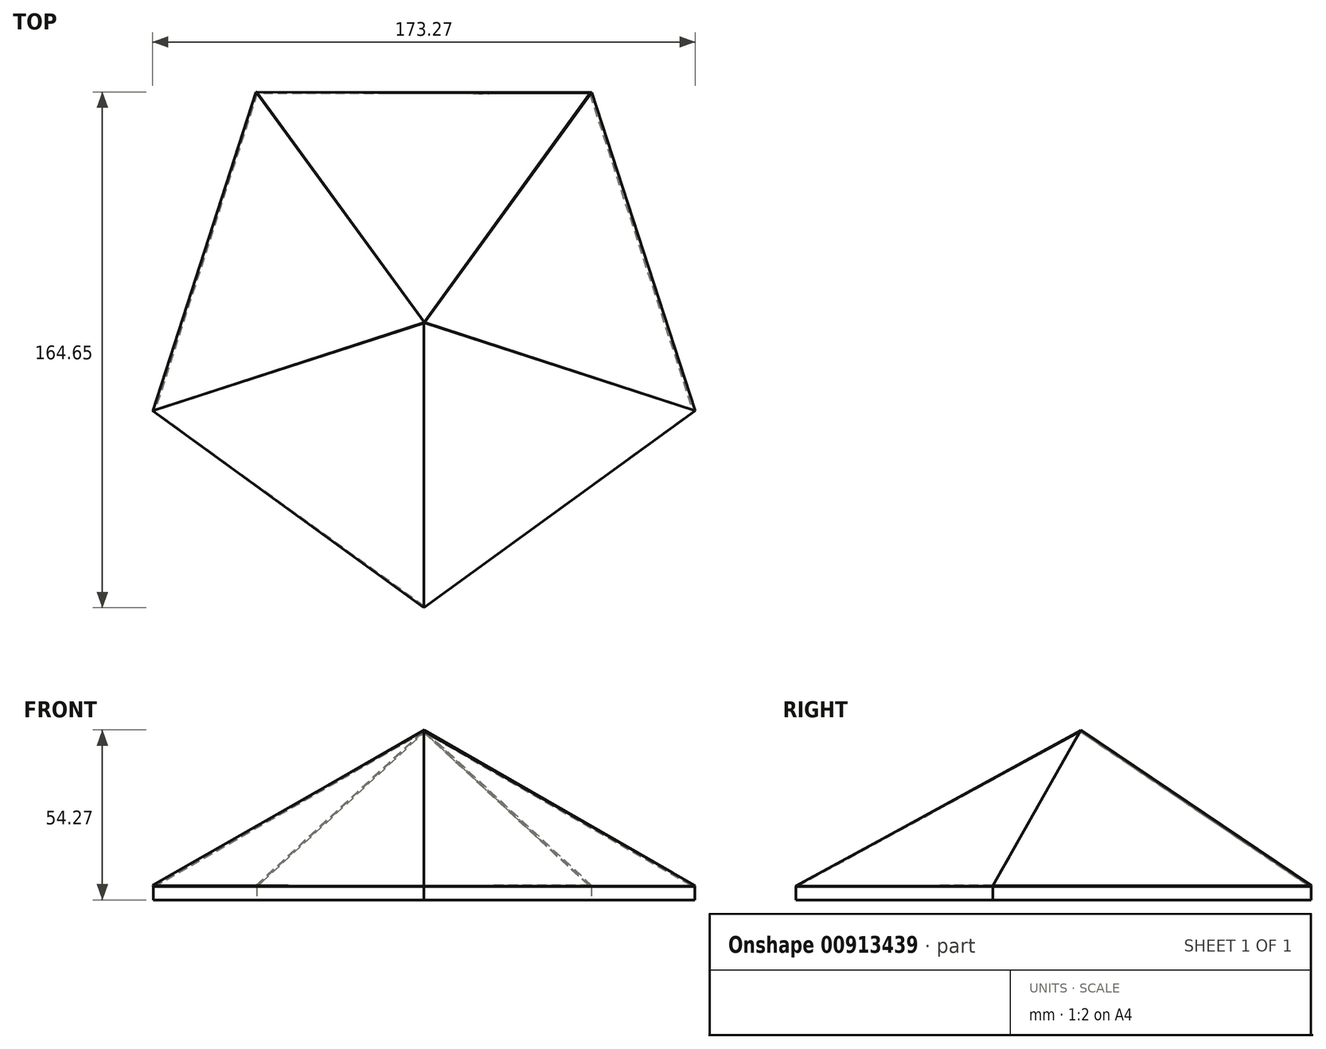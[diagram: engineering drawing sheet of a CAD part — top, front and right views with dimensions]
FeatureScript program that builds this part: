
annotation { "Feature Type Name" : "Feature", "Feature Type Description" : "" }
export const myFeature = defineFeature(function(context is Context, id is Id, definition is map)
    precondition{}
    {
        {
            var Q0;
            Q0=qCreatedBy(makeId("Top.planeOp"),FACE);
            var sketch = newSketch(context, id + "F0", { "sketchPlane" : qUnion([Q0])});
            skCircle(sketch, "E0.cCircle", {"center": v(0, 0) * mm, "radius": 73.52 * mm, "construction": true});
            skLineSegment(sketch, "E0.0", {"start": v(-53.41, 73.52) * mm, "end": v(53.41, 73.52) * mm});
            skLineSegment(sketch, "E0.1", {"start": v(53.41, 73.52) * mm, "end": v(86.43, -28.08) * mm});
            skLineSegment(sketch, "E0.2", {"start": v(86.43, -28.08) * mm, "end": v(0, -90.87) * mm});
            skLineSegment(sketch, "E0.3", {"start": v(0, -90.87) * mm, "end": v(-86.43, -28.08) * mm});
            skLineSegment(sketch, "E0.4", {"start": v(-86.43, -28.08) * mm, "end": v(-53.41, 73.52) * mm});
            skPoint(sketch, "E0.0.midPoint", {"position": v(0, 73.52) * mm});
            skSolve(sketch);
        }
        {
            var Q0;
            Q0=qCreatedBy(makeId("Front.planeOp"),FACE);
            var sketch = newSketch(context, id + "F1", { "sketchPlane" : qUnion([Q0])});
            skLineSegment(sketch, "E1", {"start": v(0, 0) * mm, "end": v(0, 53.85) * mm});
            skSolve(sketch);
        }
        {
            var Q0;
            Q0=makeQuery(id+"F0.imprint","IMPRINT",FACE,{"disambiguationData":[TD([[makeQuery(id+"F0.imprint","IMPRINT",EDGE,{"derivedFrom":sQuery(id+"F0.wireOp",EDGE,"E0.0")}),-1.0]])]});
            extrude(context, id + "F2", {"entities" : qUnion([Q0]), "depth" : 4.25 * mm, "offsetDistance" : 25.4 * mm});
        }
        {
            var Q0;
            Q0=makeQuery(id+"F2.opExtrude","CAP_VERTEX",VERTEX,{"disambiguationData":[OSD([sQuery(id+"F0.wireOp",EDGE,"E0.1"),sQuery(id+"F0.wireOp",EDGE,"E0.2")])],"isStart":false});
            var Q1;
            Q1=makeQuery(id+"F2.opExtrude","CAP_VERTEX",VERTEX,{"disambiguationData":[OSD([sQuery(id+"F0.wireOp",EDGE,"E0.0"),sQuery(id+"F0.wireOp",EDGE,"E0.1")])],"isStart":false});
            var Q2;
            Q2=sQuery(id+"F1.wireOp",VERTEX,"E1.end");
            cPlane(context, id + "F3", {"entities" : qUnion([Q0, Q1, Q2]), "cplaneType" : CPlaneType.THREE_POINT, "offset" : 25.4 * mm, "width" : 152.4 * mm, "height" : 152.4 * mm});
        }
        {
            var Q0;
            Q0=qCreatedBy(id+"F3.planeOp",FACE);
            var sketch = newSketch(context, id + "F4", { "sketchPlane" : qUnion([Q0])});
            skPoint(sketch, "E2.0", {"position": v(35.04, -71.1) * mm});
            skPoint(sketch, "E3.0", {"position": v(74.02, 28.36) * mm});
            skPoint(sketch, "E4.0", {"position": v(-28.04, 10.99) * mm});
            skLineSegment(sketch, "E5", {"start": v(74.02, 28.36) * mm, "end": v(-28.04, 10.99) * mm});
            skLineSegment(sketch, "E6", {"start": v(35.04, -71.1) * mm, "end": v(-28.04, 10.99) * mm});
            skLineSegment(sketch, "E7", {"start": v(74.02, 28.36) * mm, "end": v(35.04, -71.1) * mm});
            skSolve(sketch);
        }
        {
            var Q0;
            Q0=makeQuery(id+"F4.imprint","IMPRINT",FACE,{"disambiguationData":[TD([[makeQuery(id+"F4.imprint","IMPRINT",EDGE,{"derivedFrom":sQuery(id+"F4.wireOp",EDGE,"E5")}),1.0]])]});
            extrude(context, id + "F5", {"entities" : qUnion([Q0]), "operationType" : NewBodyOperationType.ADD, "oppositeDirection" : true, "depth" : 0.72 * mm, "offsetDistance" : 25.4 * mm, "symmetric" : true});
        }
        {
            var Q0;
            Q0=makeQuery(id+"F2.opExtrude","CAP_VERTEX",VERTEX,{"disambiguationData":[OSD([sQuery(id+"F0.wireOp",EDGE,"E0.0"),sQuery(id+"F0.wireOp",EDGE,"E0.4")])],"isStart":false});
            var Q1;
            Q1=sQuery(id+"F4.wireOp",VERTEX,"E2.0");
            var Q2;
            Q2=sQuery(id+"F4.wireOp",VERTEX,"E6.end");
            cPlane(context, id + "F6", {"entities" : qUnion([Q0, Q1, Q2]), "cplaneType" : CPlaneType.THREE_POINT, "offset" : 25.4 * mm, "width" : 152.4 * mm, "height" : 152.4 * mm});
        }
        {
            var Q0;
            Q0=qCreatedBy(id+"F6.planeOp",FACE);
            var sketch = newSketch(context, id + "F7", { "sketchPlane" : qUnion([Q0])});
            skPoint(sketch, "E8.0", {"position": v(-53.41, 58.57) * mm});
            skPoint(sketch, "E9.0", {"position": v(52.9, 58.15) * mm});
            skPoint(sketch, "E10.0", {"position": v(0, -30.11) * mm});
            skLineSegment(sketch, "E11", {"start": v(0, -30.11) * mm, "end": v(-53.41, 58.57) * mm});
            skLineSegment(sketch, "E12", {"start": v(52.9, 58.15) * mm, "end": v(-53.41, 58.57) * mm});
            skLineSegment(sketch, "E13", {"start": v(0, -30.11) * mm, "end": v(52.9, 58.15) * mm});
            skSolve(sketch);
        }
        {
            var Q0;
            Q0=makeQuery(id+"F7.imprint","IMPRINT",FACE,{"disambiguationData":[TD([[makeQuery(id+"F7.imprint","IMPRINT",EDGE,{"derivedFrom":sQuery(id+"F7.wireOp",EDGE,"E11")}),-1.0]])]});
            extrude(context, id + "F8", {"entities" : qUnion([Q0]), "operationType" : NewBodyOperationType.ADD, "depth" : 0.4 * mm, "offsetDistance" : 25.4 * mm, "symmetric" : true});
        }
        {
            var Q0;
            Q0=makeQuery(id+"F2.opExtrude","CAP_VERTEX",VERTEX,{"disambiguationData":[OSD([sQuery(id+"F0.wireOp",EDGE,"E0.3"),sQuery(id+"F0.wireOp",EDGE,"E0.4")])],"isStart":false});
            var Q1;
            Q1=makeQuery(id+"F8.opExtrude","CAP_VERTEX",VERTEX,{"disambiguationData":[OSD([sQuery(id+"F7.wireOp",EDGE,"E11"),sQuery(id+"F7.wireOp",EDGE,"E12")])],"isStart":false});
            var Q2;
            Q2=sQuery(id+"F1.wireOp",VERTEX,"E1.end");
            cPlane(context, id + "F9", {"entities" : qUnion([Q0, Q1, Q2]), "cplaneType" : CPlaneType.THREE_POINT, "offset" : 25.4 * mm, "width" : 152.4 * mm, "height" : 152.4 * mm});
        }
        {
            var Q0;
            Q0=qCreatedBy(id+"F9.planeOp",FACE);
            var sketch = newSketch(context, id + "F10", { "sketchPlane" : qUnion([Q0])});
            skPoint(sketch, "E14.0", {"position": v(-74, -28.36) * mm});
            skPoint(sketch, "E15.0", {"position": v(-35.03, 71.22) * mm});
            skPoint(sketch, "E16.0", {"position": v(28.36, -10.89) * mm});
            skLineSegment(sketch, "E17", {"start": v(-35.03, 71.22) * mm, "end": v(28.36, -10.89) * mm});
            skLineSegment(sketch, "E18", {"start": v(28.36, -10.89) * mm, "end": v(-74, -28.36) * mm});
            skLineSegment(sketch, "E19", {"start": v(-35.03, 71.22) * mm, "end": v(-74, -28.36) * mm});
            skSolve(sketch);
        }
        {
            var Q0;
            Q0=makeQuery(id+"F10.imprint","IMPRINT",FACE,{"disambiguationData":[TD([[makeQuery(id+"F10.imprint","IMPRINT",EDGE,{"derivedFrom":sQuery(id+"F10.wireOp",EDGE,"E17")}),-1.0]])]});
            extrude(context, id + "F11", {"entities" : qUnion([Q0]), "operationType" : NewBodyOperationType.ADD, "oppositeDirection" : true, "depth" : 0.6 * mm, "offsetDistance" : 25.4 * mm, "symmetric" : true});
        }
        {
            var Q0;
            Q0=makeQuery(id+"F11.opExtrude","CAP_VERTEX",VERTEX,{"disambiguationData":[OSD([sQuery(id+"F10.wireOp",EDGE,"E18"),sQuery(id+"F10.wireOp",EDGE,"E19")])],"isStart":true});
            var Q1;
            Q1=makeQuery(id+"F2.opExtrude","CAP_VERTEX",VERTEX,{"disambiguationData":[OSD([sQuery(id+"F0.wireOp",EDGE,"E0.2"),sQuery(id+"F0.wireOp",EDGE,"E0.3")])],"isStart":false});
            var Q2;
            Q2=sQuery(id+"F7.wireOp",VERTEX,"E10.0");
            cPlane(context, id + "F12", {"entities" : qUnion([Q0, Q1, Q2]), "cplaneType" : CPlaneType.THREE_POINT, "offset" : 25.4 * mm, "width" : 152.4 * mm, "height" : 152.4 * mm});
        }
        {
            var Q0;
            Q0=qCreatedBy(id+"F12.planeOp",FACE);
            var sketch = newSketch(context, id + "F13", { "sketchPlane" : qUnion([Q0])});
            skPoint(sketch, "E20.0", {"position": v(-76.18, 22.45) * mm});
            skPoint(sketch, "E21.0", {"position": v(15.42, 77.73) * mm});
            skPoint(sketch, "E22.0", {"position": v(15.42, -25.8) * mm});
            skLineSegment(sketch, "E23", {"start": v(-76.18, 22.45) * mm, "end": v(15.42, -25.8) * mm});
            skLineSegment(sketch, "E24", {"start": v(15.42, 77.73) * mm, "end": v(15.42, -25.8) * mm});
            skLineSegment(sketch, "E25", {"start": v(-76.18, 22.45) * mm, "end": v(15.42, 77.73) * mm});
            skSolve(sketch);
        }
        {
            var Q0;
            Q0=makeQuery(id+"F13.imprint","IMPRINT",FACE,{"disambiguationData":[TD([[makeQuery(id+"F13.imprint","IMPRINT",EDGE,{"derivedFrom":sQuery(id+"F13.wireOp",EDGE,"E23")}),1.0]])]});
            extrude(context, id + "F14", {"entities" : qUnion([Q0]), "operationType" : NewBodyOperationType.ADD, "oppositeDirection" : true, "depth" : 0.36 * mm, "offsetDistance" : 25.4 * mm, "symmetric" : true});
        }
        {
            var Q0;
            Q0=makeQuery(id+"F14.opExtrude","CAP_VERTEX",VERTEX,{"disambiguationData":[OSD([sQuery(id+"F13.wireOp",EDGE,"E24"),sQuery(id+"F13.wireOp",EDGE,"E25")])],"isStart":false});
            var Q1;
            Q1=makeQuery(id+"F5.opExtrude","CAP_VERTEX",VERTEX,{"disambiguationData":[OSD([sQuery(id+"F4.wireOp",EDGE,"E5"),sQuery(id+"F4.wireOp",EDGE,"E7")])],"isStart":false});
            var Q2;
            Q2=sQuery(id+"F7.wireOp",VERTEX,"E11.start");
            cPlane(context, id + "F15", {"entities" : qUnion([Q0, Q1, Q2]), "cplaneType" : CPlaneType.THREE_POINT, "offset" : 25.4 * mm, "width" : 152.4 * mm, "height" : 152.4 * mm});
        }
        {
            var Q0;
            Q0=qCreatedBy(id+"F15.planeOp",FACE);
            var sketch = newSketch(context, id + "F16", { "sketchPlane" : qUnion([Q0])});
            skPoint(sketch, "E26.0", {"position": v(-15.44, -25.73) * mm});
            skPoint(sketch, "E27.0", {"position": v(-15.5, 77.8) * mm});
            skPoint(sketch, "E28.0", {"position": v(76.2, 22.44) * mm});
            skLineSegment(sketch, "E29", {"start": v(-15.5, 77.8) * mm, "end": v(-15.44, -25.73) * mm});
            skLineSegment(sketch, "E30", {"start": v(76.2, 22.44) * mm, "end": v(-15.44, -25.73) * mm});
            skLineSegment(sketch, "E31", {"start": v(-15.5, 77.8) * mm, "end": v(76.2, 22.44) * mm});
            skSolve(sketch);
        }
        {
            var Q0;
            Q0=makeQuery(id+"F16.imprint","IMPRINT",FACE,{"disambiguationData":[TD([[makeQuery(id+"F16.imprint","IMPRINT",EDGE,{"derivedFrom":sQuery(id+"F16.wireOp",EDGE,"E29")}),1.0]])]});
            extrude(context, id + "F17", {"entities" : qUnion([Q0]), "operationType" : NewBodyOperationType.ADD, "depth" : 0.07 * mm, "offsetDistance" : 25.4 * mm, "symmetric" : true});
        }
    });
